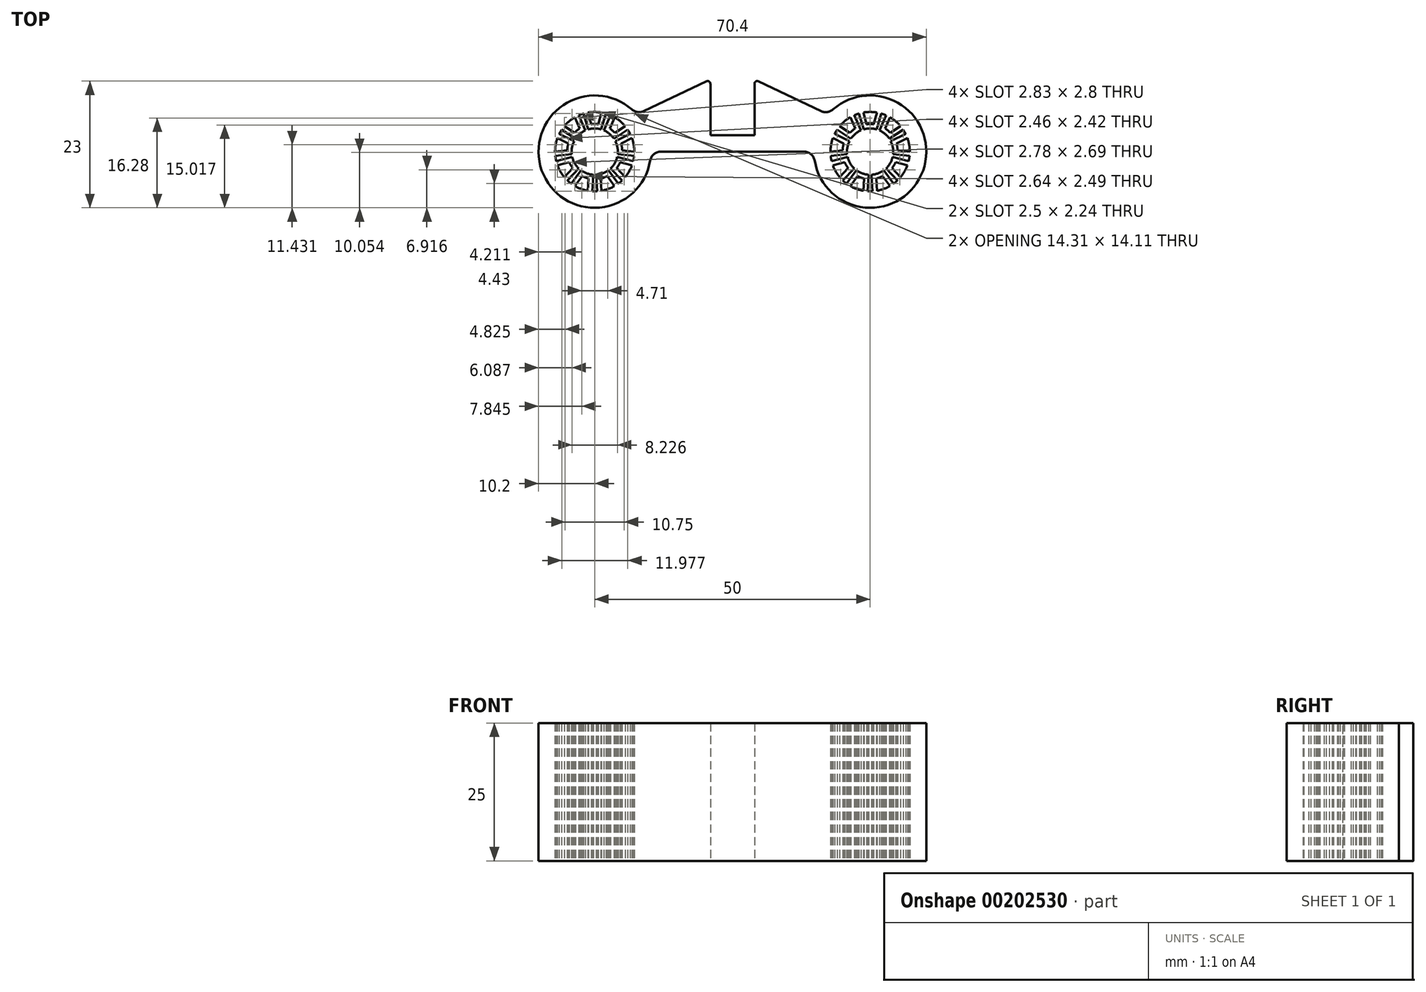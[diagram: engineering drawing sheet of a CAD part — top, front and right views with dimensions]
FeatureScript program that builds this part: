
annotation { "Feature Type Name" : "Feature", "Feature Type Description" : "" }
export const myFeature = defineFeature(function(context is Context, id is Id, definition is map)
    precondition{}
    {
        {
            var Q0;
            Q0=qCreatedBy(makeId("Top.planeOp"),FACE);
            var sketch = newSketch(context, id + "F0", { "sketchPlane" : qUnion([Q0])});
            skArc(sketch, "E0", {"start": v(1.18, 4.03) * mm, "mid": v(0, 4.2) * mm, "end": v(-1.18, 4.03) * mm});
            skArc(sketch, "E1", {"start": v(-2.03, 6.9) * mm, "mid": v(-2.46, 6.77) * mm, "end": v(-2.89, 6.6) * mm});
            skLineSegment(sketch, "E2", {"start": v(-1.18, 4.03) * mm, "end": v(-2.03, 6.9) * mm});
            skLineSegment(sketch, "E3", {"start": v(1.18, 4.03) * mm, "end": v(2.03, 6.9) * mm});
            skCircle(sketch, "E4", {"center": v(0, 0) * mm, "radius": 8 * mm});
            skLineSegment(sketch, "E5.0", {"start": v(-0.62, 4.96) * mm, "end": v(-1.25, 7.1) * mm});
            skArc(sketch, "E5.1", {"start": v(0.62, 4.96) * mm, "mid": v(0, 5) * mm, "end": v(-0.62, 4.96) * mm});
            skLineSegment(sketch, "E5.2", {"start": v(0.62, 4.96) * mm, "end": v(1.25, 7.1) * mm});
            skLineSegment(sketch, "E6.1.0", {"start": v(-3.67, 3.4) * mm, "end": v(-5.51, 4.63) * mm});
            skArc(sketch, "E6.1.1", {"start": v(-2.71, 4.2) * mm, "mid": v(-3.21, 3.83) * mm, "end": v(-3.67, 3.4) * mm});
            skLineSegment(sketch, "E6.1.2", {"start": v(-2.71, 4.2) * mm, "end": v(-3.6, 6.23) * mm});
            skLineSegment(sketch, "E6.1.3", {"start": v(-1.68, 3.85) * mm, "end": v(-2.89, 6.6) * mm});
            skArc(sketch, "E6.1.4", {"start": v(-1.68, 3.85) * mm, "mid": v(-2.7, 3.22) * mm, "end": v(-3.5, 2.33) * mm});
            skLineSegment(sketch, "E6.1.5", {"start": v(-3.5, 2.33) * mm, "end": v(-6, 3.99) * mm});
            skLineSegment(sketch, "E6.2.0", {"start": v(-5, 0.25) * mm, "end": v(-7.2, 0) * mm});
            skArc(sketch, "E6.2.1", {"start": v(-4.78, 1.47) * mm, "mid": v(-4.92, 0.87) * mm, "end": v(-5, 0.25) * mm});
            skLineSegment(sketch, "E6.2.2", {"start": v(-4.78, 1.47) * mm, "end": v(-6.77, 2.46) * mm});
            skLineSegment(sketch, "E6.2.3", {"start": v(-3.76, 1.87) * mm, "end": v(-6.45, 3.2) * mm});
            skArc(sketch, "E6.2.4", {"start": v(-3.76, 1.87) * mm, "mid": v(-4.14, 0.73) * mm, "end": v(-4.17, -0.47) * mm});
            skLineSegment(sketch, "E6.2.5", {"start": v(-4.17, -0.47) * mm, "end": v(-7.16, -0.8) * mm});
            skLineSegment(sketch, "E6.3.0", {"start": v(-3.98, -3.02) * mm, "end": v(-5.52, -4.63) * mm});
            skArc(sketch, "E6.3.1", {"start": v(-4.6, -1.94) * mm, "mid": v(-4.33, -2.5) * mm, "end": v(-3.98, -3.02) * mm});
            skLineSegment(sketch, "E6.3.2", {"start": v(-4.6, -1.94) * mm, "end": v(-6.77, -2.46) * mm});
            skLineSegment(sketch, "E6.3.3", {"start": v(-4.08, -1) * mm, "end": v(-7, -1.7) * mm});
            skArc(sketch, "E6.3.4", {"start": v(-4.08, -1) * mm, "mid": v(-3.64, -2.1) * mm, "end": v(-2.9, -3.04) * mm});
            skLineSegment(sketch, "E6.3.5", {"start": v(-2.9, -3.04) * mm, "end": v(-4.97, -5.21) * mm});
            skLineSegment(sketch, "E6.4.0", {"start": v(-1.11, -4.87) * mm, "end": v(-1.25, -7.1) * mm});
            skArc(sketch, "E6.4.1", {"start": v(-2.28, -4.45) * mm, "mid": v(-1.71, -4.7) * mm, "end": v(-1.11, -4.87) * mm});
            skLineSegment(sketch, "E6.4.2", {"start": v(-2.28, -4.45) * mm, "end": v(-3.6, -6.24) * mm});
            skLineSegment(sketch, "E6.4.3", {"start": v(-2.5, -3.38) * mm, "end": v(-4.27, -5.8) * mm});
            skArc(sketch, "E6.4.4", {"start": v(-2.5, -3.38) * mm, "mid": v(-1.44, -3.95) * mm, "end": v(-0.27, -4.2) * mm});
            skLineSegment(sketch, "E6.4.5", {"start": v(-0.27, -4.2) * mm, "end": v(-0.46, -7.19) * mm});
            skLineSegment(sketch, "E6.5.0", {"start": v(2.28, -4.45) * mm, "end": v(3.6, -6.24) * mm});
            skArc(sketch, "E6.5.1", {"start": v(1.11, -4.87) * mm, "mid": v(1.71, -4.7) * mm, "end": v(2.28, -4.45) * mm});
            skLineSegment(sketch, "E6.5.2", {"start": v(1.11, -4.87) * mm, "end": v(1.25, -7.1) * mm});
            skLineSegment(sketch, "E6.5.3", {"start": v(0.27, -4.2) * mm, "end": v(0.46, -7.19) * mm});
            skArc(sketch, "E6.5.4", {"start": v(0.27, -4.2) * mm, "mid": v(1.44, -3.95) * mm, "end": v(2.5, -3.38) * mm});
            skLineSegment(sketch, "E6.5.5", {"start": v(2.5, -3.38) * mm, "end": v(4.27, -5.8) * mm});
            skLineSegment(sketch, "E6.6.0", {"start": v(4.6, -1.94) * mm, "end": v(6.77, -2.46) * mm});
            skArc(sketch, "E6.6.1", {"start": v(3.98, -3.02) * mm, "mid": v(4.33, -2.5) * mm, "end": v(4.6, -1.94) * mm});
            skLineSegment(sketch, "E6.6.2", {"start": v(3.98, -3.02) * mm, "end": v(5.52, -4.63) * mm});
            skLineSegment(sketch, "E6.6.3", {"start": v(2.9, -3.04) * mm, "end": v(4.97, -5.21) * mm});
            skArc(sketch, "E6.6.4", {"start": v(2.9, -3.04) * mm, "mid": v(3.64, -2.1) * mm, "end": v(4.08, -1) * mm});
            skLineSegment(sketch, "E6.6.5", {"start": v(4.08, -1) * mm, "end": v(7, -1.7) * mm});
            skLineSegment(sketch, "E6.7.0", {"start": v(4.78, 1.47) * mm, "end": v(6.77, 2.46) * mm});
            skArc(sketch, "E6.7.1", {"start": v(5, 0.25) * mm, "mid": v(4.92, 0.87) * mm, "end": v(4.78, 1.47) * mm});
            skLineSegment(sketch, "E6.7.2", {"start": v(5, 0.25) * mm, "end": v(7.2, 0) * mm});
            skLineSegment(sketch, "E6.7.3", {"start": v(4.17, -0.47) * mm, "end": v(7.16, -0.8) * mm});
            skArc(sketch, "E6.7.4", {"start": v(4.17, -0.47) * mm, "mid": v(4.14, 0.73) * mm, "end": v(3.76, 1.87) * mm});
            skLineSegment(sketch, "E6.7.5", {"start": v(3.76, 1.87) * mm, "end": v(6.45, 3.2) * mm});
            skLineSegment(sketch, "E6.8.0", {"start": v(2.71, 4.2) * mm, "end": v(3.6, 6.23) * mm});
            skArc(sketch, "E6.8.1", {"start": v(3.67, 3.4) * mm, "mid": v(3.21, 3.83) * mm, "end": v(2.71, 4.2) * mm});
            skLineSegment(sketch, "E6.8.2", {"start": v(3.67, 3.4) * mm, "end": v(5.51, 4.63) * mm});
            skLineSegment(sketch, "E6.8.3", {"start": v(3.5, 2.33) * mm, "end": v(6, 3.99) * mm});
            skArc(sketch, "E6.8.4", {"start": v(3.5, 2.33) * mm, "mid": v(2.7, 3.22) * mm, "end": v(1.68, 3.85) * mm});
            skLineSegment(sketch, "E6.8.5", {"start": v(1.68, 3.85) * mm, "end": v(2.89, 6.6) * mm});
            skArc(sketch, "E7.trimOffspring", {"start": v(1.25, 7.1) * mm, "mid": v(0, 7.2) * mm, "end": v(-1.25, 7.1) * mm});
            skArc(sketch, "E8.trimOffspring", {"start": v(2.89, 6.6) * mm, "mid": v(2.46, 6.77) * mm, "end": v(2.03, 6.9) * mm});
            skArc(sketch, "E9.trimOffspring", {"start": v(5.51, 4.63) * mm, "mid": v(4.63, 5.52) * mm, "end": v(3.6, 6.23) * mm});
            skArc(sketch, "E10.trimOffspring", {"start": v(6.45, 3.2) * mm, "mid": v(6.24, 3.6) * mm, "end": v(6, 3.99) * mm});
            skArc(sketch, "E11.trimOffspring", {"start": v(7.2, 0) * mm, "mid": v(7.1, 1.25) * mm, "end": v(6.77, 2.46) * mm});
            skArc(sketch, "E12.trimOffspring", {"start": v(-3.6, 6.23) * mm, "mid": v(-4.63, 5.52) * mm, "end": v(-5.51, 4.63) * mm});
            skArc(sketch, "E13.trimOffspring", {"start": v(-6, 3.99) * mm, "mid": v(-6.24, 3.6) * mm, "end": v(-6.45, 3.2) * mm});
            skArc(sketch, "E14.trimOffspring", {"start": v(-6.77, 2.46) * mm, "mid": v(-7.1, 1.25) * mm, "end": v(-7.2, 0) * mm});
            skArc(sketch, "E15.trimOffspring", {"start": v(-7.16, -0.8) * mm, "mid": v(-7.1, -1.25) * mm, "end": v(-7, -1.7) * mm});
            skArc(sketch, "E16.trimOffspring", {"start": v(-6.77, -2.46) * mm, "mid": v(-6.24, -3.6) * mm, "end": v(-5.52, -4.63) * mm});
            skArc(sketch, "E17.trimOffspring", {"start": v(-4.97, -5.21) * mm, "mid": v(-4.63, -5.52) * mm, "end": v(-4.27, -5.8) * mm});
            skArc(sketch, "E18.trimOffspring", {"start": v(-3.6, -6.24) * mm, "mid": v(-2.46, -6.77) * mm, "end": v(-1.25, -7.1) * mm});
            skArc(sketch, "E19.trimOffspring", {"start": v(-0.46, -7.19) * mm, "mid": v(0, -7.2) * mm, "end": v(0.46, -7.19) * mm});
            skArc(sketch, "E20.trimOffspring", {"start": v(1.25, -7.1) * mm, "mid": v(2.46, -6.77) * mm, "end": v(3.6, -6.24) * mm});
            skArc(sketch, "E21.trimOffspring", {"start": v(4.27, -5.8) * mm, "mid": v(4.63, -5.52) * mm, "end": v(4.97, -5.21) * mm});
            skArc(sketch, "E22.trimOffspring", {"start": v(5.52, -4.63) * mm, "mid": v(6.24, -3.6) * mm, "end": v(6.77, -2.46) * mm});
            skArc(sketch, "E23.trimOffspring", {"start": v(7, -1.7) * mm, "mid": v(7.1, -1.25) * mm, "end": v(7.16, -0.8) * mm});
            skSolve(sketch);
        }
        {
            var Q0;
            Q0 = qSketchRegion(id + "F0", true);
            extrude(context, id + "F1", {"entities" : qUnion([Q0]), "depth" : 25 * mm});
        }
        {
            var Q0;
            Q0=qCreatedBy(makeId("Right.planeOp"),FACE);
            cPlane(context, id + "F2", {"entities" : qUnion([Q0]), "cplaneType" : CPlaneType.OFFSET, "offset" : 25 * mm, "width" : 150 * mm, "height" : 150 * mm});
        }
        {
            var Q0;
            Q0=makeQuery(id+"F1.opExtrude","SWEPT_BODY",BODY,{"disambiguationData":[OSD([sQuery(id+"F0.wireOp",EDGE,"E0"),sQuery(id+"F0.wireOp",EDGE,"E1"),sQuery(id+"F0.wireOp",EDGE,"E2"),sQuery(id+"F0.wireOp",EDGE,"E3"),sQuery(id+"F0.wireOp",EDGE,"E4"),sQuery(id+"F0.wireOp",EDGE,"E5.0"),sQuery(id+"F0.wireOp",EDGE,"E5.1"),sQuery(id+"F0.wireOp",EDGE,"E5.2"),sQuery(id+"F0.wireOp",EDGE,"E6.1.0"),sQuery(id+"F0.wireOp",EDGE,"E6.1.1"),sQuery(id+"F0.wireOp",EDGE,"E6.1.2"),sQuery(id+"F0.wireOp",EDGE,"E6.1.3"),sQuery(id+"F0.wireOp",EDGE,"E6.1.4"),sQuery(id+"F0.wireOp",EDGE,"E6.1.5"),sQuery(id+"F0.wireOp",EDGE,"E6.2.0"),sQuery(id+"F0.wireOp",EDGE,"E6.2.1"),sQuery(id+"F0.wireOp",EDGE,"E6.2.2"),sQuery(id+"F0.wireOp",EDGE,"E6.2.3"),sQuery(id+"F0.wireOp",EDGE,"E6.2.4"),sQuery(id+"F0.wireOp",EDGE,"E6.2.5"),sQuery(id+"F0.wireOp",EDGE,"E6.3.0"),sQuery(id+"F0.wireOp",EDGE,"E6.3.1"),sQuery(id+"F0.wireOp",EDGE,"E6.3.2"),sQuery(id+"F0.wireOp",EDGE,"E6.3.3"),sQuery(id+"F0.wireOp",EDGE,"E6.3.4"),sQuery(id+"F0.wireOp",EDGE,"E6.3.5"),sQuery(id+"F0.wireOp",EDGE,"E6.4.0"),sQuery(id+"F0.wireOp",EDGE,"E6.4.1"),sQuery(id+"F0.wireOp",EDGE,"E6.4.2"),sQuery(id+"F0.wireOp",EDGE,"E6.4.3"),sQuery(id+"F0.wireOp",EDGE,"E6.4.4"),sQuery(id+"F0.wireOp",EDGE,"E6.4.5"),sQuery(id+"F0.wireOp",EDGE,"E6.5.0"),sQuery(id+"F0.wireOp",EDGE,"E6.5.1"),sQuery(id+"F0.wireOp",EDGE,"E6.5.2"),sQuery(id+"F0.wireOp",EDGE,"E6.5.3"),sQuery(id+"F0.wireOp",EDGE,"E6.5.4"),sQuery(id+"F0.wireOp",EDGE,"E6.5.5"),sQuery(id+"F0.wireOp",EDGE,"E6.6.0"),sQuery(id+"F0.wireOp",EDGE,"E6.6.1"),sQuery(id+"F0.wireOp",EDGE,"E6.6.2"),sQuery(id+"F0.wireOp",EDGE,"E6.6.3"),sQuery(id+"F0.wireOp",EDGE,"E6.6.4"),sQuery(id+"F0.wireOp",EDGE,"E6.6.5"),sQuery(id+"F0.wireOp",EDGE,"E6.7.0"),sQuery(id+"F0.wireOp",EDGE,"E6.7.1"),sQuery(id+"F0.wireOp",EDGE,"E6.7.2"),sQuery(id+"F0.wireOp",EDGE,"E6.7.3"),sQuery(id+"F0.wireOp",EDGE,"E6.7.4"),sQuery(id+"F0.wireOp",EDGE,"E6.7.5"),sQuery(id+"F0.wireOp",EDGE,"E6.8.0"),sQuery(id+"F0.wireOp",EDGE,"E6.8.1"),sQuery(id+"F0.wireOp",EDGE,"E6.8.2"),sQuery(id+"F0.wireOp",EDGE,"E6.8.3"),sQuery(id+"F0.wireOp",EDGE,"E6.8.4"),sQuery(id+"F0.wireOp",EDGE,"E6.8.5"),sQuery(id+"F0.wireOp",EDGE,"E7.trimOffspring"),sQuery(id+"F0.wireOp",EDGE,"E8.trimOffspring"),sQuery(id+"F0.wireOp",EDGE,"E9.trimOffspring"),sQuery(id+"F0.wireOp",EDGE,"E10.trimOffspring"),sQuery(id+"F0.wireOp",EDGE,"E11.trimOffspring"),sQuery(id+"F0.wireOp",EDGE,"E12.trimOffspring"),sQuery(id+"F0.wireOp",EDGE,"E13.trimOffspring"),sQuery(id+"F0.wireOp",EDGE,"E14.trimOffspring"),sQuery(id+"F0.wireOp",EDGE,"E15.trimOffspring"),sQuery(id+"F0.wireOp",EDGE,"E16.trimOffspring"),sQuery(id+"F0.wireOp",EDGE,"E17.trimOffspring"),sQuery(id+"F0.wireOp",EDGE,"E18.trimOffspring"),sQuery(id+"F0.wireOp",EDGE,"E19.trimOffspring"),sQuery(id+"F0.wireOp",EDGE,"E20.trimOffspring"),sQuery(id+"F0.wireOp",EDGE,"E21.trimOffspring"),sQuery(id+"F0.wireOp",EDGE,"E22.trimOffspring"),sQuery(id+"F0.wireOp",EDGE,"E23.trimOffspring")])]});
            var Q1;
            Q1=qCreatedBy(id+"F2.planeOp",FACE);
            mirror(context, id + "F3", {"entities" : qUnion([Q0]), "mirrorPlane" : qUnion([Q1])});
        }
        {
            var Q0;
            Q0=qCreatedBy(makeId("Top.planeOp"),FACE);
            var sketch = newSketch(context, id + "F4", { "sketchPlane" : qUnion([Q0])});
            skCircle(sketch, "E24", {"center": v(0, 0) * mm, "radius": 7.5 * mm});
            skLineSegment(sketch, "E25", {"start": v(10.2, 0) * mm, "end": v(39.8, 0) * mm});
            skCircle(sketch, "E26.MirrorC", {"center": v(50, 0) * mm, "radius": 7.5 * mm});
            skLineSegment(sketch, "E27", {"start": v(25, 0) * mm, "end": v(25, 15) * mm, "construction": true});
            skLineSegment(sketch, "E28", {"start": v(21, 13.1) * mm, "end": v(7.66, 6.74) * mm});
            skLineSegment(sketch, "E29", {"start": v(29, 13.1) * mm, "end": v(42.34, 6.74) * mm});
            skPoint(sketch, "E30.orphan", {"position": v(4, 5) * mm});
            skPoint(sketch, "E31.orphan", {"position": v(46, 5) * mm});
            skArc(sketch, "E32", {"start": v(7.66, 6.74) * mm, "mid": v(-9.54, -3.6) * mm, "end": v(10.2, 0) * mm});
            skArc(sketch, "E33", {"start": v(39.8, 0) * mm, "mid": v(59.54, -3.6) * mm, "end": v(42.34, 6.74) * mm});
            skPoint(sketch, "E34.orphan", {"position": v(7.5, 0) * mm});
            skPoint(sketch, "E35.orphan", {"position": v(42.5, 0) * mm});
            skLineSegment(sketch, "E36.top", {"start": v(21, 3) * mm, "end": v(29, 3) * mm});
            skLineSegment(sketch, "E36.left", {"start": v(21, 13.1) * mm, "end": v(21, 3) * mm});
            skLineSegment(sketch, "E36.right", {"start": v(29, 13.1) * mm, "end": v(29, 3) * mm});
            skSolve(sketch);
        }
        {
            var Q0;
            Q0 = qSketchRegion(id + "F4", true);
            extrude(context, id + "F5", {"entities" : qUnion([Q0]), "operationType" : NewBodyOperationType.ADD, "depth" : 25 * mm});
        }
        {
            var Q0;
            Q0=makeQuery(id+"F5.opExtrude","SWEPT_EDGE",EDGE,{"disambiguationData":[OSD([sQuery(id+"F4.wireOp",EDGE,"E28"),sQuery(id+"F4.wireOp",EDGE,"E36.left")])]});
            var Q1;
            Q1=makeQuery(id+"F5.opExtrude","SWEPT_EDGE",EDGE,{"disambiguationData":[OSD([sQuery(id+"F4.wireOp",EDGE,"E29"),sQuery(id+"F4.wireOp",EDGE,"E36.right")])]});
            fillet(context, id + "F6", {"entities" : qUnion([Q0, Q1]), "radius" : 0.5 * mm, "tangentPropagation" : true, "allowEdgeOverflow" : false});
        }
        {
            var Q0;
            Q0=makeQuery(id+"F5.opExtrude","SWEPT_EDGE",EDGE,{"disambiguationData":[OSD([sQuery(id+"F4.wireOp",EDGE,"E25"),sQuery(id+"F4.wireOp",EDGE,"E32")])]});
            var Q1;
            Q1=makeQuery(id+"F5.opExtrude","SWEPT_EDGE",EDGE,{"disambiguationData":[OSD([sQuery(id+"F4.wireOp",EDGE,"E25"),sQuery(id+"F4.wireOp",EDGE,"E33")])]});
            var Q2;
            Q2=makeQuery(id+"F5.opExtrude","SWEPT_EDGE",EDGE,{"disambiguationData":[OSD([sQuery(id+"F4.wireOp",EDGE,"E28"),sQuery(id+"F4.wireOp",EDGE,"E32")])]});
            var Q3;
            Q3=makeQuery(id+"F5.opExtrude","SWEPT_EDGE",EDGE,{"disambiguationData":[OSD([sQuery(id+"F4.wireOp",EDGE,"E29"),sQuery(id+"F4.wireOp",EDGE,"E33")])]});
            fillet(context, id + "F7", {"entities" : qUnion([Q0, Q1, Q2, Q3]), "radius" : 2 * mm, "tangentPropagation" : true, "allowEdgeOverflow" : false});
        }
    });
